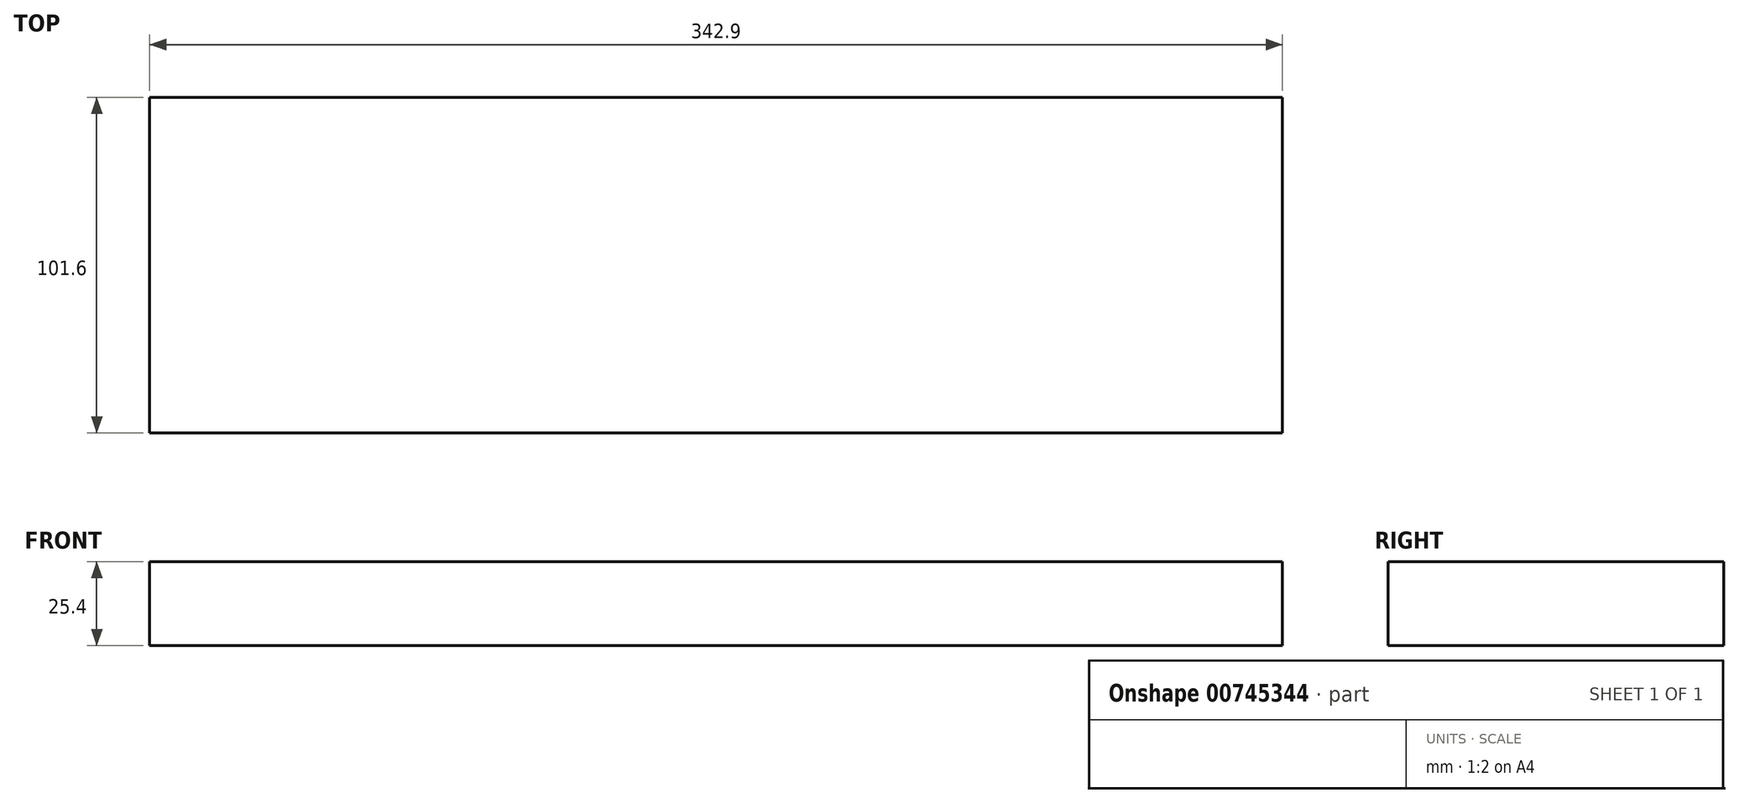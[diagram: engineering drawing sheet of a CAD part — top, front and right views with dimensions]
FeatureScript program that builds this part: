
annotation { "Feature Type Name" : "Feature", "Feature Type Description" : "" }
export const myFeature = defineFeature(function(context is Context, id is Id, definition is map)
    precondition{}
    {
        {
            var Q0;
            Q0=qCreatedBy(makeId("Top.planeOp"),FACE);
            var sketch = newSketch(context, id + "F0", { "sketchPlane" : qUnion([Q0])});
            skLineSegment(sketch, "E0.bottom", {"start": v(0, 0) * mm, "end": v(342.9, 0) * mm});
            skLineSegment(sketch, "E0.top", {"start": v(0, 101.6) * mm, "end": v(342.9, 101.6) * mm});
            skLineSegment(sketch, "E0.left", {"start": v(0, 0) * mm, "end": v(0, 101.6) * mm});
            skLineSegment(sketch, "E0.right", {"start": v(342.9, 0) * mm, "end": v(342.9, 101.6) * mm});
            skSolve(sketch);
        }
        {
            var Q0;
            Q0=makeQuery(id+"F0.imprint","IMPRINT",FACE,{"disambiguationData":[TD([[makeQuery(id+"F0.imprint","IMPRINT",EDGE,{"derivedFrom":sQuery(id+"F0.wireOp",EDGE,"E0.bottom")}),1.0]])]});
            extrude(context, id + "F1", {"entities" : qUnion([Q0]), "depth" : 25.4 * mm, "offsetDistance" : 25.4 * mm});
        }
    });
